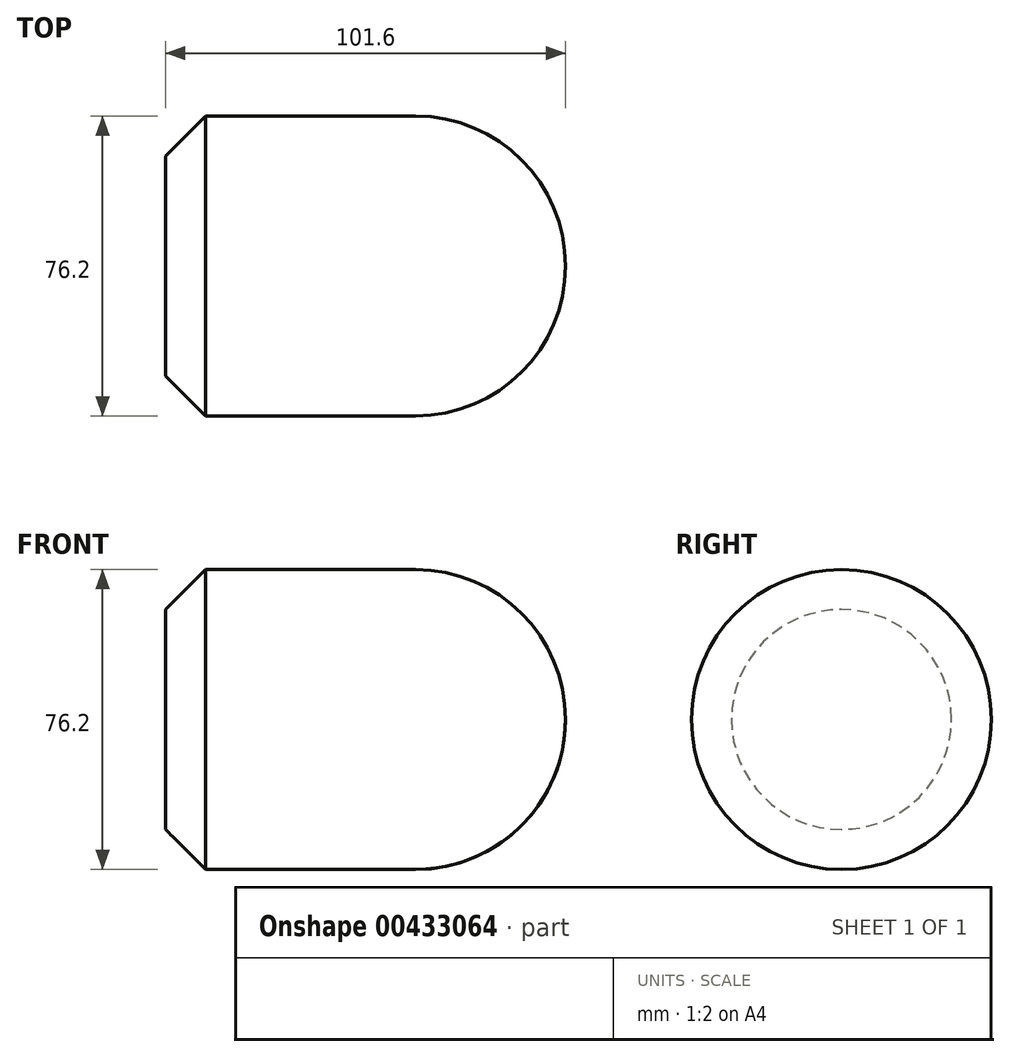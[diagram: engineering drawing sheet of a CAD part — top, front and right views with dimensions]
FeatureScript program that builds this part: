
annotation { "Feature Type Name" : "Feature", "Feature Type Description" : "" }
export const myFeature = defineFeature(function(context is Context, id is Id, definition is map)
    precondition{}
    {
        {
            var Q0;
            Q0=qCreatedBy(makeId("Right.planeOp"),FACE);
            var sketch = newSketch(context, id + "F0", { "sketchPlane" : qUnion([Q0])});
            skCircle(sketch, "E0", {"center": v(0, 0) * mm, "radius": 38.1 * mm});
            skSolve(sketch);
        }
        {
            var Q0;
            Q0 = qSketchRegion(id + "F0", true);
            extrude(context, id + "F1", {"entities" : qUnion([Q0]), "depth" : 101.6 * mm});
        }
        {
            var Q0;
            Q0=makeQuery(id+"F1.opExtrude","CAP_EDGE",EDGE,{"disambiguationData":[OSD([sQuery(id+"F0.wireOp",EDGE,"E0")])],"isStart":false});
            fillet(context, id + "F2", {"entities" : qUnion([Q0]), "radius" : 38.1 * mm, "tangentPropagation" : true, "allowEdgeOverflow" : false});
        }
        {
            var Q0;
            Q0=makeQuery(id+"F1.opExtrude","CAP_EDGE",EDGE,{"disambiguationData":[OSD([sQuery(id+"F0.wireOp",EDGE,"E0")])],"isStart":true});
            chamfer(context, id + "F3", {"entities" : qUnion([Q0]), "width" : 10.16 * mm, "tangentPropagation" : true});
        }
    });
